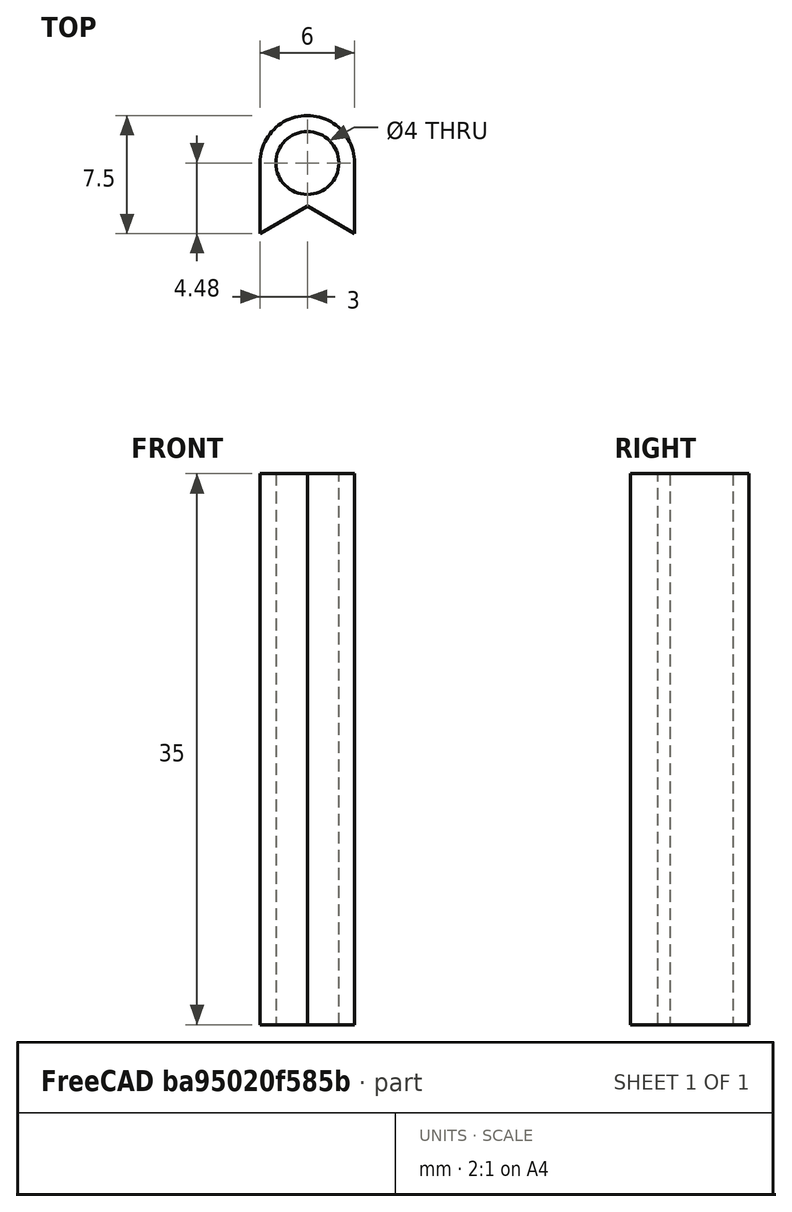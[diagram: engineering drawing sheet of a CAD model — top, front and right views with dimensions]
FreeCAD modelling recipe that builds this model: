
FCSTD DOCUMENT  (FreeCAD 0.21R33771 (Git))
Label: 4mm_hole_rail_lug
License: All rights reserved
LicenseURL: http://en.wikipedia.org/wiki/All_rights_reserved
objects: Sketcher::SketchObject×1, PartDesign::Pad×1, PartDesign::Body×1
note: 4 computed .brp shape members not serialized (recipe doc carries the construction recipe); baked Part::Feature solids carry a one-line shape summary decoded from their .brp

FEATURE [Sketcher::SketchObject] Sketch
  FullyConstrained = true
  MapMode = 5
  Support = -> [XY_Plane]
  sketch-geometry (6):
    g0: Circle CenterX=0 CenterY=0 CenterZ=0 NormalX=0 NormalY=0 NormalZ=1 AngleXU=0 Radius=2
    g1: LineSegment StartX=3 StartY=0.0179593 StartZ=0 EndX=3 EndY=-4.48204 EndZ=0
    g2: LineSegment StartX=-3 StartY=-4.48206 StartZ=0 EndX=-3 EndY=0.0179391 EndZ=0
    g3: LineSegment StartX=0 StartY=-2.75 StartZ=0 EndX=-3 EndY=-4.48206 EndZ=0
    g4: LineSegment StartX=0 StartY=-2.75 StartZ=0 EndX=3 EndY=-4.48204 EndZ=0
    g5: ArcOfCircle CenterX=-1e-16 CenterY=0.0179593 CenterZ=0 NormalX=0 NormalY=0 NormalZ=1 AngleXU=0 Radius=3 StartAngle=1e-16 EndAngle=3.1416
  constraints (17):
    c: Coincident(g0,g-1)
    c: Radius(g0) = 2
    c: Vertical(g1)
    c: Vertical(g2)
    c: PointOnObject(g3,g-2)
    c: Coincident(g3,g2)
    c: Coincident(g3,g4)
    c: Coincident(g4,g1)
    c: Angle(g3,g4) = 2.0944
    c: Coincident(g5,g2)
    c: Tangent(g5,g1) = 1.5708
    c: DistanceY(g3,g0) = 2.75
    c: DistanceX(g2,g0) = 3
    c: DistanceX(g0,g1) = 3
    c: DistanceY(g1,g1) = 4.5
    c: DistanceY(g2,g2) = 4.5
    c: Radius(g5) = 3
FEATURE [PartDesign::Pad] Pad
  Direction = (0,0,1)
  Length = 35
  Length2 = 10
  Profile = -> Sketch
  ReferenceAxis = -> Sketch [N_Axis]
  Type = 0
FEATURE [PartDesign::Body] Body
  Group = -> [Sketch,Pad]
  Origin = -> Origin
  Tip = -> Pad
